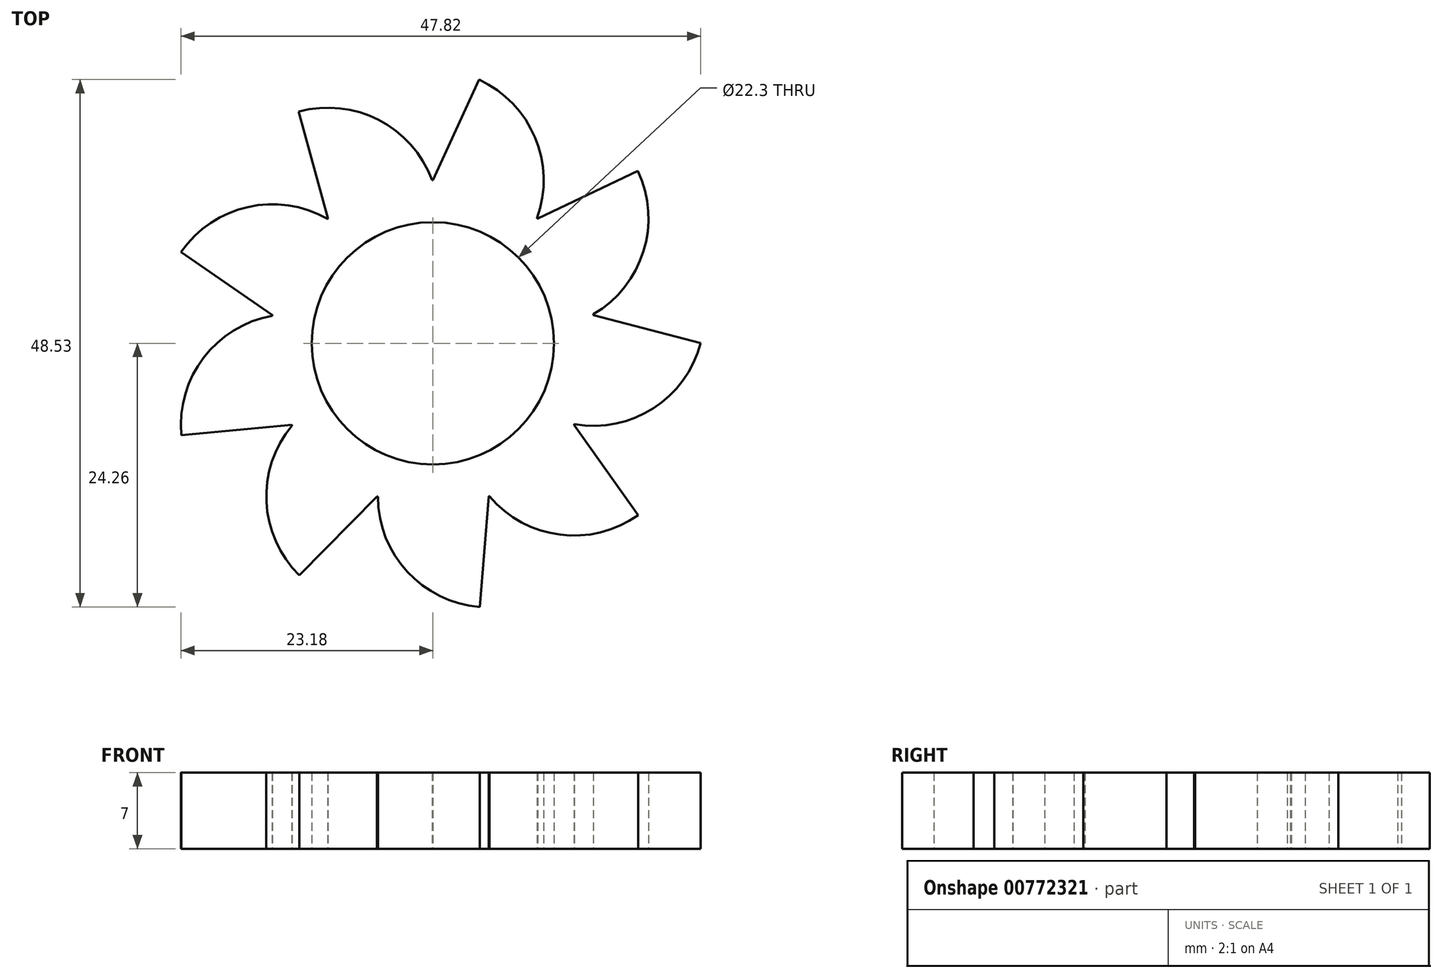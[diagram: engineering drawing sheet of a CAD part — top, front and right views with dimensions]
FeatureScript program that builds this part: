
annotation { "Feature Type Name" : "Feature", "Feature Type Description" : "" }
export const myFeature = defineFeature(function(context is Context, id is Id, definition is map)
    precondition{}
    {
        {
            var Q0;
            Q0=qCreatedBy(makeId("Top.planeOp"),FACE);
            var sketch = newSketch(context, id + "F0", { "sketchPlane" : qUnion([Q0])});
            skCircle(sketch, "E0", {"center": v(0, 0) * mm, "radius": 11.15 * mm});
            skCircle(sketch, "E1", {"center": v(0, 0) * mm, "radius": 15 * mm});
            skLineSegment(sketch, "E2", {"start": v(0, 15) * mm, "end": v(4.42, 24.67) * mm});
            skArc(sketch, "E3", {"start": v(9.59, 11.54) * mm, "mid": v(9.4, 18.95) * mm, "end": v(4.24, 24.27) * mm});
            skLineSegment(sketch, "E4.1.0", {"start": v(-9.64, 11.5) * mm, "end": v(-12.47, 21.74) * mm});
            skArc(sketch, "E4.1.1", {"start": v(-0.07, 15) * mm, "mid": v(-4.98, 20.56) * mm, "end": v(-12.35, 21.32) * mm});
            skLineSegment(sketch, "E4.2.0", {"start": v(-14.77, 2.6) * mm, "end": v(-23.52, 8.64) * mm});
            skArc(sketch, "E4.2.1", {"start": v(-9.7, 11.44) * mm, "mid": v(-17.03, 12.55) * mm, "end": v(-23.16, 8.4) * mm});
            skLineSegment(sketch, "E4.3.0", {"start": v(-13, -7.5) * mm, "end": v(-23.57, -8.5) * mm});
            skArc(sketch, "E4.3.1", {"start": v(-14.78, 2.53) * mm, "mid": v(-21.1, -1.33) * mm, "end": v(-23.14, -8.46) * mm});
            skLineSegment(sketch, "E4.4.0", {"start": v(-5.13, -14.1) * mm, "end": v(-12.6, -21.67) * mm});
            skArc(sketch, "E4.4.1", {"start": v(-12.95, -7.56) * mm, "mid": v(-15.31, -14.59) * mm, "end": v(-12.29, -21.36) * mm});
            skLineSegment(sketch, "E4.5.0", {"start": v(5.13, -14.1) * mm, "end": v(4.28, -24.69) * mm});
            skArc(sketch, "E4.5.1", {"start": v(-5.06, -14.12) * mm, "mid": v(-2.35, -21.02) * mm, "end": v(4.32, -24.26) * mm});
            skLineSegment(sketch, "E4.6.0", {"start": v(13, -7.5) * mm, "end": v(19.15, -16.16) * mm});
            skArc(sketch, "E4.6.1", {"start": v(5.2, -14.07) * mm, "mid": v(11.7, -17.61) * mm, "end": v(18.9, -15.8) * mm});
            skLineSegment(sketch, "E4.7.0", {"start": v(14.77, 2.6) * mm, "end": v(25.06, -0.07) * mm});
            skArc(sketch, "E4.7.1", {"start": v(13.03, -7.44) * mm, "mid": v(20.3, -5.97) * mm, "end": v(24.64, 0.04) * mm});
            skLineSegment(sketch, "E4.8.0", {"start": v(9.64, 11.5) * mm, "end": v(19.24, 16.05) * mm});
            skArc(sketch, "E4.8.1", {"start": v(14.76, 2.67) * mm, "mid": v(19.38, 8.47) * mm, "end": v(18.85, 15.87) * mm});
            skSolve(sketch);
        }
        {
            var Q0;
            Q0 = qSketchRegion(id + "F0", true);
            extrude(context, id + "F1", {"entities" : qUnion([Q0]), "depth" : 7 * mm, "offsetDistance" : 25 * mm});
        }
    });
